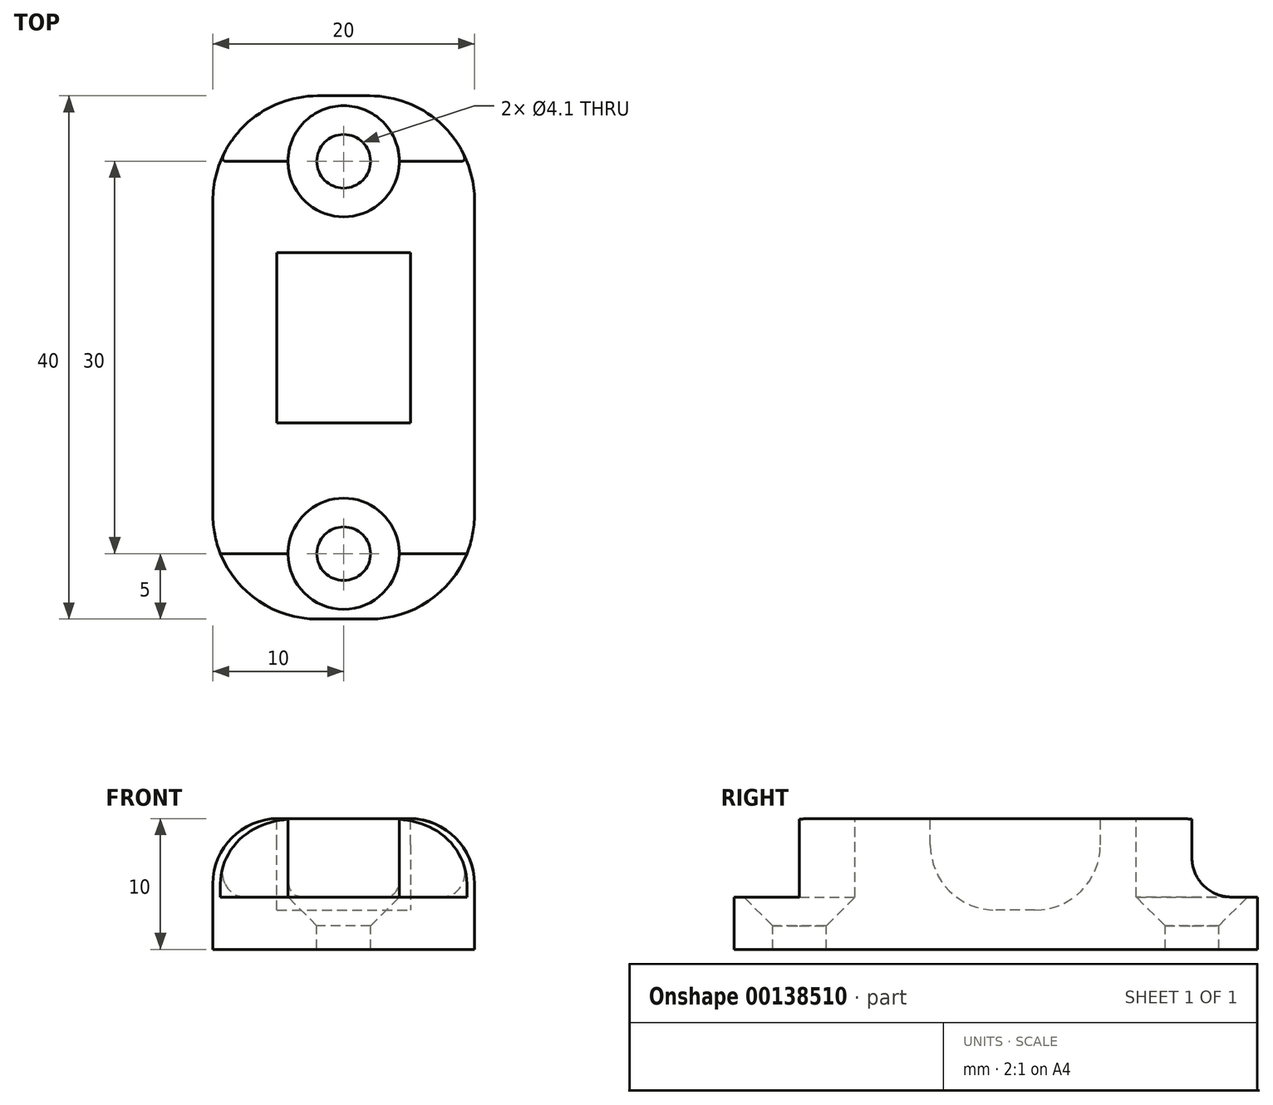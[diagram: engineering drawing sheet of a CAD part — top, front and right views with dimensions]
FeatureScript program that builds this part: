
annotation { "Feature Type Name" : "Feature", "Feature Type Description" : "" }
export const myFeature = defineFeature(function(context is Context, id is Id, definition is map)
    precondition{}
    {
        {
            var Q0;
            Q0=qCreatedBy(makeId("Top.planeOp"),FACE);
            var sketch = newSketch(context, id + "F0", { "sketchPlane" : qUnion([Q0])});
            skLineSegment(sketch, "E0.bottom", {"start": v(0, 0) * mm, "end": v(-20, 0) * mm});
            skLineSegment(sketch, "E0.top", {"start": v(0, 30) * mm, "end": v(-20, 30) * mm});
            skLineSegment(sketch, "E0.left", {"start": v(0, 0) * mm, "end": v(0, 30) * mm});
            skLineSegment(sketch, "E0.right", {"start": v(-20, 0) * mm, "end": v(-20, 30) * mm});
            skSolve(sketch);
        }
        {
            var Q0;
            Q0 = qSketchRegion(id + "F0", true);
            extrude(context, id + "F1", {"entities" : qUnion([Q0]), "depth" : 6 * mm});
        }
        {
            var Q0;
            Q0=qCreatedBy(makeId("Top.planeOp"),FACE);
            var sketch = newSketch(context, id + "F2", { "sketchPlane" : qUnion([Q0])});
            skLineSegment(sketch, "E1.bottom", {"start": v(0, -5) * mm, "end": v(-20, -5) * mm});
            skLineSegment(sketch, "E1.top", {"start": v(0, 35) * mm, "end": v(-20, 35) * mm});
            skLineSegment(sketch, "E1.left", {"start": v(0, -5) * mm, "end": v(0, 35) * mm});
            skLineSegment(sketch, "E1.right", {"start": v(-20, -5) * mm, "end": v(-20, 35) * mm});
            skSolve(sketch);
        }
        {
            var Q0;
            Q0 = qSketchRegion(id + "F2", true);
            extrude(context, id + "F3", {"entities" : qUnion([Q0]), "operationType" : NewBodyOperationType.ADD, "oppositeDirection" : true, "depth" : 4 * mm});
        }
        {
            var Q0;
            Q0=makeQuery(id+"F1.opExtrude","CAP_FACE",FACE,{"disambiguationData":[OSD([sQuery(id+"F0.wireOp",EDGE,"E0.bottom"),sQuery(id+"F0.wireOp",EDGE,"E0.top"),sQuery(id+"F0.wireOp",EDGE,"E0.left"),sQuery(id+"F0.wireOp",EDGE,"E0.right")])],"isStart":false});
            cPlane(context, id + "F4", {"entities" : qUnion([Q0]), "cplaneType" : CPlaneType.OFFSET, "offset" : 0 * mm, "width" : 150 * mm, "height" : 150 * mm});
        }
        {
            var Q0;
            Q0=qCreatedBy(id+"F4.planeOp",FACE);
            var sketch = newSketch(context, id + "F5", { "sketchPlane" : qUnion([Q0])});
            skLineSegment(sketch, "E2.bottom", {"start": v(-15.1, 23) * mm, "end": v(-4.9, 23) * mm});
            skLineSegment(sketch, "E2.top", {"start": v(-15.1, 10) * mm, "end": v(-4.9, 10) * mm});
            skLineSegment(sketch, "E2.left", {"start": v(-15.1, 23) * mm, "end": v(-15.1, 10) * mm});
            skLineSegment(sketch, "E2.right", {"start": v(-4.9, 23) * mm, "end": v(-4.9, 10) * mm});
            skSolve(sketch);
        }
        {
            var Q0;
            Q0 = qSketchRegion(id + "F5", true);
            extrude(context, id + "F6", {"entities" : qUnion([Q0]), "operationType" : NewBodyOperationType.REMOVE, "oppositeDirection" : true, "depth" : 7 * mm});
        }
        {
            var Q0;
            Q0=makeQuery(id+"F6.boolean.opBoolean","COPY",EDGE,{"derivedFrom":makeQuery(id+"F6.opExtrude","CAP_EDGE",EDGE,{"disambiguationData":[OSD([sQuery(id+"F5.wireOp",EDGE,"E2.bottom")])],"isStart":false})});
            var Q1;
            Q1=makeQuery(id+"F6.boolean.opBoolean","COPY",EDGE,{"derivedFrom":makeQuery(id+"F6.opExtrude","CAP_EDGE",EDGE,{"disambiguationData":[OSD([sQuery(id+"F5.wireOp",EDGE,"E2.top")])],"isStart":false})});
            fillet(context, id + "F7", {"entities" : qUnion([Q0, Q1]), "radius" : 5 * mm, "tangentPropagation" : true, "allowEdgeOverflow" : false});
        }
        {
            var Q0;
            Q0=qCreatedBy(id+"F4.planeOp",FACE);
            var sketch = newSketch(context, id + "F8", { "sketchPlane" : qUnion([Q0])});
            skPoint(sketch, "E3", {"position": v(-10, 30) * mm});
            skPoint(sketch, "E4", {"position": v(-10, 0) * mm});
            skSolve(sketch);
        }
        {
            var Q0;
            Q0=sQuery(id+"F8.wireOp",VERTEX,"E3");
            var Q1;
            Q1=sQuery(id+"F8.wireOp",VERTEX,"E4");
            var Q2;
            Q2=makeQuery(id+"F1.opExtrude","SWEPT_BODY",BODY,{"disambiguationData":[OSD([sQuery(id+"F0.wireOp",EDGE,"E0.bottom"),sQuery(id+"F0.wireOp",EDGE,"E0.top"),sQuery(id+"F0.wireOp",EDGE,"E0.left"),sQuery(id+"F0.wireOp",EDGE,"E0.right")])]});
            hole(context, id + "F9", {"style" : HoleStyle.C_SINK, "endStyle" : HoleEndStyle.THROUGH, "holeDiameter" : 4.1 * mm, "cSinkDiameter" : 8.5 * mm, "cSinkAngle" : 90 * degree, "locations" : qUnion([Q0, Q1]), "scope" : qUnion([Q2]), "isTappedThrough" : true});
        }
        {
            var Q0;
            Q0=makeQuery(id+"F3.opExtrude","SWEPT_EDGE",EDGE,{"disambiguationData":[OSD([sQuery(id+"F2.wireOp",EDGE,"E1.bottom"),sQuery(id+"F2.wireOp",EDGE,"E1.right")])]});
            var Q1;
            Q1=makeQuery(id+"F3.opExtrude","SWEPT_EDGE",EDGE,{"disambiguationData":[OSD([sQuery(id+"F2.wireOp",EDGE,"E1.bottom"),sQuery(id+"F2.wireOp",EDGE,"E1.left")])]});
            var Q2;
            Q2=makeQuery(id+"F3.opExtrude","SWEPT_EDGE",EDGE,{"disambiguationData":[OSD([sQuery(id+"F2.wireOp",EDGE,"E1.top"),sQuery(id+"F2.wireOp",EDGE,"E1.right")])]});
            var Q3;
            Q3=makeQuery(id+"F3.opExtrude","SWEPT_EDGE",EDGE,{"disambiguationData":[OSD([sQuery(id+"F2.wireOp",EDGE,"E1.top"),sQuery(id+"F2.wireOp",EDGE,"E1.left")])]});
            fillet(context, id + "F10", {"entities" : qUnion([Q0, Q1, Q2, Q3]), "radius" : 8 * mm, "tangentPropagation" : true, "allowEdgeOverflow" : false});
        }
        {
            var Q0;
            {var subQ1=sQuery(id+"F0.wireOp",EDGE,"E0.bottom");Q0=makeQuery(id+"F9.hole-1.boolean.opBoolean","SPLIT",EDGE,{"disambiguationData":[TD([makeQuery(id+"F1.opExtrude","SWEPT_FACE",FACE,{"disambiguationData":[OSD([sQuery(id+"F0.wireOp",EDGE,"E0.right")])]})])],"derivedFrom":makeQuery(id+"F1.opExtrude","CAP_EDGE",EDGE,{"disambiguationData":[OSD([subQ1])],"isStart":true})});}
            var Q1;
            {var subQ1=sQuery(id+"F0.wireOp",EDGE,"E0.bottom");Q1=makeQuery(id+"F9.hole-1.boolean.opBoolean","SPLIT",EDGE,{"disambiguationData":[TD([makeQuery(id+"F1.opExtrude","SWEPT_FACE",FACE,{"disambiguationData":[OSD([sQuery(id+"F0.wireOp",EDGE,"E0.left")])]})])],"derivedFrom":makeQuery(id+"F1.opExtrude","CAP_EDGE",EDGE,{"disambiguationData":[OSD([subQ1])],"isStart":true})});}
            var Q2;
            {var subQ1=sQuery(id+"F0.wireOp",EDGE,"E0.top");Q2=makeQuery(id+"F9.hole-0.boolean.opBoolean","SPLIT",EDGE,{"disambiguationData":[TD([makeQuery(id+"F1.opExtrude","SWEPT_FACE",FACE,{"disambiguationData":[OSD([sQuery(id+"F0.wireOp",EDGE,"E0.left")])]})])],"derivedFrom":makeQuery(id+"F1.opExtrude","CAP_EDGE",EDGE,{"disambiguationData":[OSD([subQ1])],"isStart":true})});}
            var Q3;
            {var subQ1=sQuery(id+"F0.wireOp",EDGE,"E0.top");Q3=makeQuery(id+"F9.hole-0.boolean.opBoolean","SPLIT",EDGE,{"disambiguationData":[TD([makeQuery(id+"F1.opExtrude","SWEPT_FACE",FACE,{"disambiguationData":[OSD([sQuery(id+"F0.wireOp",EDGE,"E0.right")])]})])],"derivedFrom":makeQuery(id+"F1.opExtrude","CAP_EDGE",EDGE,{"disambiguationData":[OSD([subQ1])],"isStart":true})});}
            fillet(context, id + "F11", {"entities" : qUnion([Q0, Q1, Q2, Q3]), "radius" : 3 * mm, "tangentPropagation" : true, "allowEdgeOverflow" : false});
        }
        {
            var Q0;
            {var subQ0=sQuery(id+"F0.wireOp",EDGE,"E0.left");var subQ1=sQuery(id+"F0.wireOp",EDGE,"E0.bottom");Q0=makeQuery(id+"F9.hole-1.boolean.opBoolean","SPLIT",EDGE,{"disambiguationData":[TD([makeQuery(id+"F1.opExtrude","SWEPT_FACE",FACE,{"disambiguationData":[OSD([subQ0])]})])],"derivedFrom":makeQuery(id+"F1.opExtrude","CAP_EDGE",EDGE,{"disambiguationData":[OSD([subQ1])],"isStart":false})});}
            var Q1;
            {var subQ0=sQuery(id+"F0.wireOp",EDGE,"E0.left");var subQ1=sQuery(id+"F0.wireOp",EDGE,"E0.top");Q1=makeQuery(id+"F9.hole-0.boolean.opBoolean","SPLIT",EDGE,{"disambiguationData":[TD([makeQuery(id+"F1.opExtrude","SWEPT_FACE",FACE,{"disambiguationData":[OSD([subQ0])]})])],"derivedFrom":makeQuery(id+"F1.opExtrude","CAP_EDGE",EDGE,{"disambiguationData":[OSD([subQ1])],"isStart":false})});}
            var Q2;
            {var subQ0=sQuery(id+"F0.wireOp",EDGE,"E0.right");var subQ1=sQuery(id+"F0.wireOp",EDGE,"E0.top");Q2=makeQuery(id+"F9.hole-0.boolean.opBoolean","SPLIT",EDGE,{"disambiguationData":[TD([makeQuery(id+"F1.opExtrude","SWEPT_FACE",FACE,{"disambiguationData":[OSD([subQ0])]})])],"derivedFrom":makeQuery(id+"F1.opExtrude","CAP_EDGE",EDGE,{"disambiguationData":[OSD([subQ1])],"isStart":false})});}
            var Q3;
            {var subQ0=sQuery(id+"F0.wireOp",EDGE,"E0.right");var subQ1=sQuery(id+"F0.wireOp",EDGE,"E0.bottom");Q3=makeQuery(id+"F9.hole-1.boolean.opBoolean","SPLIT",EDGE,{"disambiguationData":[TD([makeQuery(id+"F1.opExtrude","SWEPT_FACE",FACE,{"disambiguationData":[OSD([subQ0])]})])],"derivedFrom":makeQuery(id+"F1.opExtrude","CAP_EDGE",EDGE,{"disambiguationData":[OSD([subQ1])],"isStart":false})});}
            var Q4;
            Q4=makeQuery(id+"F1.opExtrude","CAP_EDGE",EDGE,{"disambiguationData":[OSD([sQuery(id+"F0.wireOp",EDGE,"E0.left")])],"isStart":false});
            var Q5;
            Q5=makeQuery(id+"F1.opExtrude","CAP_EDGE",EDGE,{"disambiguationData":[OSD([sQuery(id+"F0.wireOp",EDGE,"E0.right")])],"isStart":false});
            fillet(context, id + "F12", {"entities" : qUnion([Q0, Q1, Q2, Q3, Q4, Q5]), "radius" : 5 * mm, "tangentPropagation" : true, "allowEdgeOverflow" : false});
        }
    });
